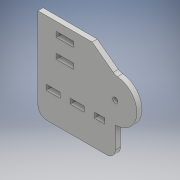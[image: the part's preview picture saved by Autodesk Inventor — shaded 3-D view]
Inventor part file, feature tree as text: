
AUTODESK INVENTOR PART (.ipt)
format: ipt  version: 2018 (Build 220112000, 112)  size: 152,064 bytes
history: native  units: mm
features: extrude x2, sketch x2, other x1
ambient origin geometry x8: Origin, YZ Plane, XZ Plane, XY Plane, X Axis, Y Axis, Z Axis, Center Point
bodies: Body1 (feature_tree)
feature tree (5):
  other  "Sólido1"
  extrude  "Extrusión1"  Depth=16.0mm
  extrude  "Extrusión2"  Depth=6.0mm
  sketch  "Boceto1"  dims[d26=30.0mm d125=16.0mm]
  sketch  "Boceto2"  dims[d165=8.0mm d166=6.0mm d167=8.0mm d169=6.0mm d170=5.0mm d172=3.0mm d173=0.0mm d175=10.0mm d176=0.0mm]
